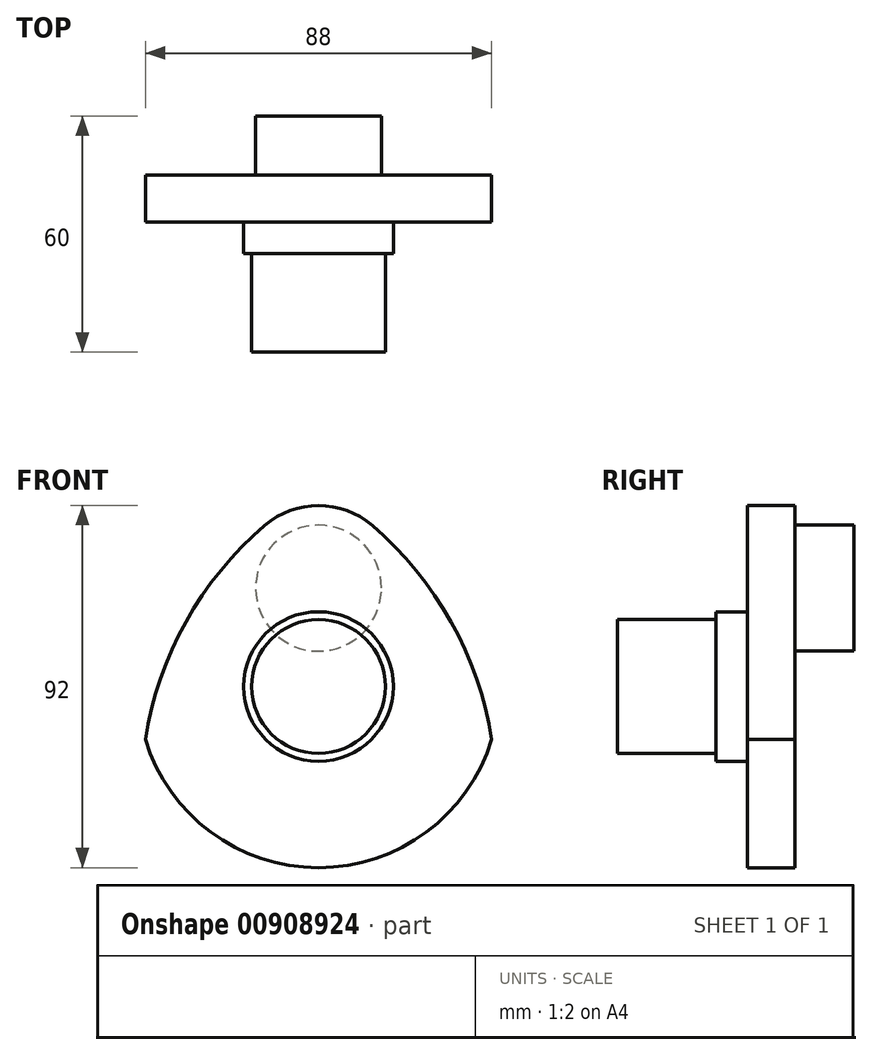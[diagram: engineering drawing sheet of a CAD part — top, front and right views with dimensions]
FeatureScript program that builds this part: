
annotation { "Feature Type Name" : "Feature", "Feature Type Description" : "" }
export const myFeature = defineFeature(function(context is Context, id is Id, definition is map)
    precondition{}
    {
        {
            var Q0;
            Q0=qCreatedBy(makeId("Front.planeOp"),FACE);
            var sketch = newSketch(context, id + "F0", { "sketchPlane" : qUnion([Q0])});
            skCircle(sketch, "E0", {"center": v(0, 0) * mm, "radius": 17 * mm});
            skSolve(sketch);
        }
        {
            var Q0;
            Q0 = qSketchRegion(id + "F0", true);
            extrude(context, id + "F1", {"entities" : qUnion([Q0]), "depth" : 25 * mm, "offsetDistance" : 25 * mm});
        }
        {
            var Q0;
            Q0=qCreatedBy(makeId("Front.planeOp"),FACE);
            var sketch = newSketch(context, id + "F2", { "sketchPlane" : qUnion([Q0])});
            skCircle(sketch, "E1", {"center": v(0, 0) * mm, "radius": 19 * mm});
            skSolve(sketch);
        }
        {
            var Q0;
            Q0 = qSketchRegion(id + "F2", true);
            extrude(context, id + "F3", {"entities" : qUnion([Q0]), "operationType" : NewBodyOperationType.ADD, "oppositeDirection" : true, "depth" : 8 * mm, "offsetDistance" : 25 * mm});
        }
        {
            var Q0;
            Q0=makeQuery(id+"F3.opExtrude","CAP_FACE",FACE,{"disambiguationData":[OSD([sQuery(id+"F2.wireOp",EDGE,"E1")])],"isStart":false});
            var sketch = newSketch(context, id + "F4", { "sketchPlane" : qUnion([Q0])});
            skArc(sketch, "E2", {"start": v(-44, -13.42) * mm, "mid": v(0, -46) * mm, "end": v(44, -13.42) * mm});
            skArc(sketch, "E3", {"start": v(13.67, 40.94) * mm, "mid": v(0, 46) * mm, "end": v(-13.67, 40.94) * mm});
            skArc(sketch, "E4", {"start": v(-13.67, 40.94) * mm, "mid": v(-33.68, 16.47) * mm, "end": v(-44, -13.42) * mm});
            skArc(sketch, "E5", {"start": v(44, -13.42) * mm, "mid": v(33.68, 16.47) * mm, "end": v(13.67, 40.94) * mm});
            skSolve(sketch);
        }
        {
            var Q0;
            Q0 = qSketchRegion(id + "F4", true);
            extrude(context, id + "F5", {"entities" : qUnion([Q0]), "operationType" : NewBodyOperationType.ADD, "depth" : 12 * mm, "offsetDistance" : 25 * mm});
        }
        {
            var Q0;
            Q0=makeQuery(id+"F5.opExtrude","CAP_FACE",FACE,{"disambiguationData":[OSD([sQuery(id+"F4.wireOp",EDGE,"E2"),sQuery(id+"F4.wireOp",EDGE,"E3"),sQuery(id+"F4.wireOp",EDGE,"E4"),sQuery(id+"F4.wireOp",EDGE,"E5")])],"isStart":false});
            var sketch = newSketch(context, id + "F6", { "sketchPlane" : qUnion([Q0])});
            skCircle(sketch, "E6", {"center": v(0, 25) * mm, "radius": 16 * mm});
            skSolve(sketch);
        }
        {
            var Q0;
            Q0 = qSketchRegion(id + "F6", true);
            extrude(context, id + "F7", {"entities" : qUnion([Q0]), "operationType" : NewBodyOperationType.ADD, "depth" : 15 * mm, "offsetDistance" : 25 * mm});
        }
    });
